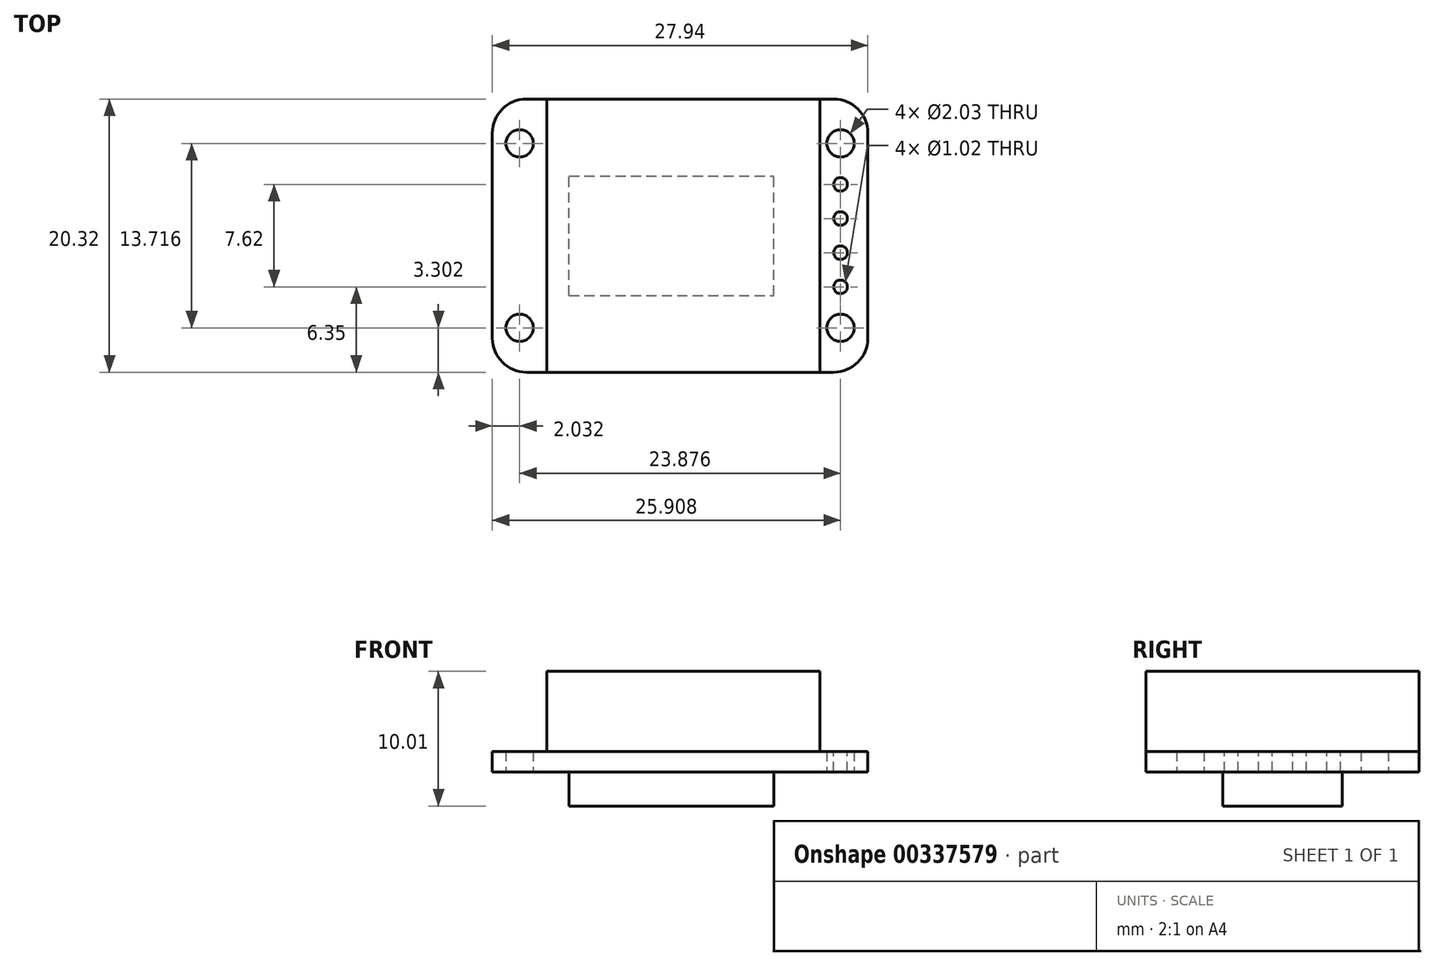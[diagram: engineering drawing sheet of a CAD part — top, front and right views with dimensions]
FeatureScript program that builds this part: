
annotation { "Feature Type Name" : "Feature", "Feature Type Description" : "" }
export const myFeature = defineFeature(function(context is Context, id is Id, definition is map)
    precondition{}
    {
        {
            var Q0;
            Q0=qCreatedBy(makeId("Top.planeOp"),FACE);
            var sketch = newSketch(context, id + "F0", { "sketchPlane" : qUnion([Q0])});
            skLineSegment(sketch, "E0.bottom", {"start": v(13.97, -10.16) * mm, "end": v(-13.97, -10.16) * mm});
            skLineSegment(sketch, "E0.top", {"start": v(13.97, 10.16) * mm, "end": v(-13.97, 10.16) * mm});
            skLineSegment(sketch, "E0.left", {"start": v(13.97, -10.16) * mm, "end": v(13.97, 10.16) * mm});
            skLineSegment(sketch, "E0.right", {"start": v(-13.97, -10.16) * mm, "end": v(-13.97, 10.16) * mm});
            skPoint(sketch, "E0.middle", {"position": v(0, 0) * mm});
            skLineSegment(sketch, "E1.bottom", {"start": v(11.94, -6.86) * mm, "end": v(-11.94, -6.86) * mm, "construction": true});
            skLineSegment(sketch, "E1.top", {"start": v(11.94, 6.86) * mm, "end": v(-11.94, 6.86) * mm, "construction": true});
            skLineSegment(sketch, "E1.left", {"start": v(11.94, -6.86) * mm, "end": v(11.94, 6.86) * mm, "construction": true});
            skLineSegment(sketch, "E1.right", {"start": v(-11.94, -6.86) * mm, "end": v(-11.94, 6.86) * mm, "construction": true});
            skCircle(sketch, "E2", {"center": v(11.94, -6.86) * mm, "radius": 1.02 * mm});
            skCircle(sketch, "E3", {"center": v(11.94, 6.86) * mm, "radius": 1.02 * mm});
            skCircle(sketch, "E4", {"center": v(-11.94, -6.86) * mm, "radius": 1.02 * mm});
            skCircle(sketch, "E5", {"center": v(-11.94, 6.86) * mm, "radius": 1.02 * mm});
            skSolve(sketch);
        }
        {
            var Q0;
            Q0 = qSketchRegion(id + "F0", true);
            extrude(context, id + "F1", {"entities" : qUnion([Q0]), "depth" : 1.52 * mm});
        }
        {
            var Q0;
            Q0=makeQuery(id+"F1.opExtrude","SWEPT_EDGE",EDGE,{"disambiguationData":[OSD([sQuery(id+"F0.wireOp",EDGE,"E0.bottom"),sQuery(id+"F0.wireOp",EDGE,"E0.left")])]});
            var Q1;
            Q1=makeQuery(id+"F1.opExtrude","SWEPT_EDGE",EDGE,{"disambiguationData":[OSD([sQuery(id+"F0.wireOp",EDGE,"E0.bottom"),sQuery(id+"F0.wireOp",EDGE,"E0.right")])]});
            var Q2;
            Q2=makeQuery(id+"F1.opExtrude","SWEPT_EDGE",EDGE,{"disambiguationData":[OSD([sQuery(id+"F0.wireOp",EDGE,"E0.top"),sQuery(id+"F0.wireOp",EDGE,"E0.right")])]});
            var Q3;
            Q3=makeQuery(id+"F1.opExtrude","SWEPT_EDGE",EDGE,{"disambiguationData":[OSD([sQuery(id+"F0.wireOp",EDGE,"E0.top"),sQuery(id+"F0.wireOp",EDGE,"E0.left")])]});
            fillet(context, id + "F2", {"entities" : qUnion([Q0, Q1, Q2, Q3]), "radius" : 2.54 * mm, "tangentPropagation" : true, "allowEdgeOverflow" : false});
        }
        {
            var Q0;
            Q0=makeQuery(id+"F1.opExtrude","CAP_FACE",FACE,{"disambiguationData":[OSD([sQuery(id+"F0.wireOp",EDGE,"E0.bottom"),sQuery(id+"F0.wireOp",EDGE,"E0.top"),sQuery(id+"F0.wireOp",EDGE,"E0.left"),sQuery(id+"F0.wireOp",EDGE,"E0.right"),sQuery(id+"F0.wireOp",EDGE,"E2"),sQuery(id+"F0.wireOp",EDGE,"E3"),sQuery(id+"F0.wireOp",EDGE,"E4"),sQuery(id+"F0.wireOp",EDGE,"E5")])],"isStart":false});
            var sketch = newSketch(context, id + "F3", { "sketchPlane" : qUnion([Q0])});
            skLineSegment(sketch, "E6.bottom", {"start": v(10.41, -10.16) * mm, "end": v(-9.9, -10.16) * mm});
            skLineSegment(sketch, "E6.top", {"start": v(10.41, 10.16) * mm, "end": v(-9.9, 10.16) * mm});
            skLineSegment(sketch, "E6.left", {"start": v(10.41, -10.16) * mm, "end": v(10.41, 10.16) * mm});
            skLineSegment(sketch, "E6.right", {"start": v(-9.9, -10.16) * mm, "end": v(-9.9, 10.16) * mm});
            skPoint(sketch, "E6.middle", {"position": v(0.25, 0) * mm});
            skSolve(sketch);
        }
        {
            var Q0;
            Q0 = qSketchRegion(id + "F3", true);
            extrude(context, id + "F4", {"entities" : qUnion([Q0]), "depth" : 5.94 * mm});
        }
        {
            var Q0;
            Q0=makeQuery(id+"F1.opExtrude","CAP_FACE",FACE,{"disambiguationData":[OSD([sQuery(id+"F0.wireOp",EDGE,"E0.bottom"),sQuery(id+"F0.wireOp",EDGE,"E0.top"),sQuery(id+"F0.wireOp",EDGE,"E0.left"),sQuery(id+"F0.wireOp",EDGE,"E0.right"),sQuery(id+"F0.wireOp",EDGE,"E2"),sQuery(id+"F0.wireOp",EDGE,"E3"),sQuery(id+"F0.wireOp",EDGE,"E4"),sQuery(id+"F0.wireOp",EDGE,"E5")])],"isStart":false});
            var sketch = newSketch(context, id + "F5", { "sketchPlane" : qUnion([Q0])});
            skCircle(sketch, "E7", {"center": v(11.94, 3.81) * mm, "radius": 0.5 * mm});
            skLineSegment(sketch, "E8", {"start": v(11.94, 6.86) * mm, "end": v(11.94, 3.81) * mm, "construction": true});
            skLineSegment(sketch, "E9", {"start": v(11.94, 1.27) * mm, "end": v(11.94, -1.27) * mm, "construction": true});
            skLineSegment(sketch, "E10", {"start": v(11.94, -1.27) * mm, "end": v(11.94, -3.81) * mm, "construction": true});
            skLineSegment(sketch, "E11", {"start": v(11.94, -3.81) * mm, "end": v(11.94, -6.86) * mm, "construction": true});
            skLineSegment(sketch, "E12", {"start": v(11.94, 1.27) * mm, "end": v(11.94, 3.81) * mm, "construction": true});
            skCircle(sketch, "E13", {"center": v(11.94, 1.27) * mm, "radius": 0.5 * mm});
            skCircle(sketch, "E14", {"center": v(11.94, -1.27) * mm, "radius": 0.5 * mm});
            skCircle(sketch, "E15", {"center": v(11.94, -3.81) * mm, "radius": 0.5 * mm});
            skSolve(sketch);
        }
        {
            var Q0;
            Q0 = qSketchRegion(id + "F5", true);
            extrude(context, id + "F6", {"entities" : qUnion([Q0]), "operationType" : NewBodyOperationType.REMOVE, "endBound" : BoundingType.THROUGH_ALL, "oppositeDirection" : true, "depth" : 25.4 * mm});
        }
        {
            var Q0;
            Q0=makeQuery(id+"F1.opExtrude","CAP_FACE",FACE,{"disambiguationData":[OSD([sQuery(id+"F0.wireOp",EDGE,"E0.bottom"),sQuery(id+"F0.wireOp",EDGE,"E0.top"),sQuery(id+"F0.wireOp",EDGE,"E0.left"),sQuery(id+"F0.wireOp",EDGE,"E0.right"),sQuery(id+"F0.wireOp",EDGE,"E2"),sQuery(id+"F0.wireOp",EDGE,"E3"),sQuery(id+"F0.wireOp",EDGE,"E4"),sQuery(id+"F0.wireOp",EDGE,"E5")])],"isStart":true});
            var sketch = newSketch(context, id + "F7", { "sketchPlane" : qUnion([Q0])});
            skLineSegment(sketch, "E16.bottom", {"start": v(-8.26, 4.44) * mm, "end": v(6.99, 4.45) * mm});
            skLineSegment(sketch, "E16.top", {"start": v(-8.25, -4.45) * mm, "end": v(6.99, -4.44) * mm});
            skLineSegment(sketch, "E16.left", {"start": v(-8.26, 4.44) * mm, "end": v(-8.25, -4.45) * mm});
            skLineSegment(sketch, "E16.right", {"start": v(6.98, 4.45) * mm, "end": v(6.99, -4.44) * mm});
            skPoint(sketch, "E16.middle", {"position": v(-0.64, 0) * mm});
            skSolve(sketch);
        }
        {
            var Q0;
            Q0 = qSketchRegion(id + "F7", true);
            extrude(context, id + "F8", {"entities" : qUnion([Q0]), "operationType" : NewBodyOperationType.ADD, "depth" : 2.54 * mm});
        }
    });
